# Revit family: Dryer_Weight-Rated_Milnor_M115-Electric
name_source: partatom
category: Mechanical Equipment
units: mm (PartAtom-declared; Revit-internal decimal feet)

## family parameters
Always vertical = No
Classification Number = 23.45.70.11.14.17
Cut with Voids When Loaded = No
Maintain Annotation Orientation = No
Part Type = Normal
Room Calculation Point = No
Round Connector Dimension = Use Radius
Shared = No
Work Plane-Based = Yes

## types (1)
- Dryer_Weight-Rated_Milnor_M115-Electric
    Air Flow = 0 CFM
    Assembly Code = E1010610
    Circuit Breaker Size = 0 A
    Cylinder Depth = 3' - 5 1/4"
    Cylinder Diameter = 3' - 6"
    Cylinder Volume = 0 CF
    Default Elevation = 0' - 0"
    Door Base from FF = 2' - 3 1/2"
    Door Opening = 2' - 7 3/8"
    Door Opening Depth = 3' - 1 7/8"
    Door Thickness = 0' - 2"
    Electrical CL from CL = 0' - 2"
    Electrical CL from FF = 6' - 0 1/2"
    Electrical CL from Side = 1' - 1 3/4"
    Exhaust CL from FF = 1' - 2 9/16"
    Exhaust CL from Side = 0' - 8 1/4"
    Exhaust Diameter = 1' - 2"
    Expected Lifespan (Years) = 0
    FSS Water Connection CL from FF = 5' - 7 3/8"
    FSS Water Connection Diameter = 0' - 0 3/4"
    FSS Water Connection from Side = 0' - 2 3/4"
    Frequency = 0 Hz
    Heat Input = 0.0 Btu/h
    Keynote = 11110
    MEP Amperage = 0 A
    Maintenance Schedule (Months) = 0
    Manufacturer = Pellerin Milnor Corp
    Manufacturer Fax = 504-468-3094
    Manufacturer Website = http://www.milnor.com
    Model = As Specified
    Number of Poles = 1
    Number of Wires = 0
    Oven Depth = 4' - 9 9/16"
    Oven Height = 1' - 2"
    Oven Width = 2' - 0"
    Oven kW Size = 0 W
    Phase = 0
    Product Data = http://www.arcat.com
    Reversing = Yes
    Revision = R1_04-2011
    Sales Information = http://www.milnor.com
    Send Message = http://www.arcat.com
    URL = http://www.milnor.com
    Unit Depth = 5' - 1 5/16"
    Unit Height = 8' - 2"
    Unit Weight = 0
    Unit Width = 3' - 10 1/8"
    Voltage_MEP = 0 V
    Warranty Duration (Years) = 0
    exhaustrad = 0' - 7"
    fsswaterrad = 0' - 0 3/8"

## geometry (parser evidence)
native form markers: Sweep x2
no freeform markers — native parametric forms only
